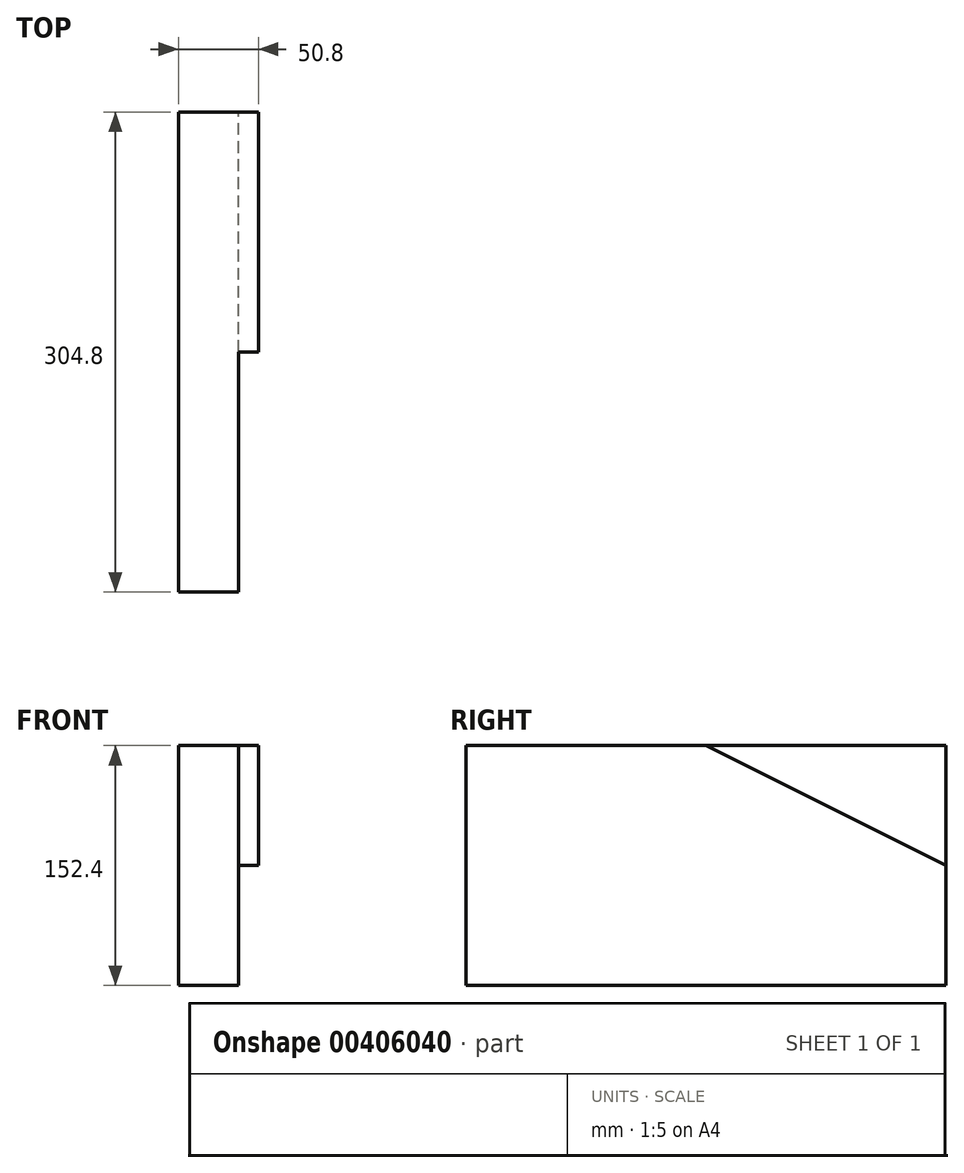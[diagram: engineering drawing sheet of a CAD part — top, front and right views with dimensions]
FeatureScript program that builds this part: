
annotation { "Feature Type Name" : "Feature", "Feature Type Description" : "" }
export const myFeature = defineFeature(function(context is Context, id is Id, definition is map)
    precondition{}
    {
        {
            var Q0;
            Q0=qCreatedBy(makeId("Right.planeOp"),FACE);
            var sketch = newSketch(context, id + "F0", { "sketchPlane" : qUnion([Q0])});
            skLineSegment(sketch, "E0.bottom", {"start": v(152.4, -76.2) * mm, "end": v(-152.4, -76.2) * mm});
            skLineSegment(sketch, "E0.top", {"start": v(152.4, 76.2) * mm, "end": v(-152.4, 76.2) * mm});
            skLineSegment(sketch, "E0.left", {"start": v(152.4, -76.2) * mm, "end": v(152.4, 76.2) * mm});
            skLineSegment(sketch, "E0.right", {"start": v(-152.4, -76.2) * mm, "end": v(-152.4, 76.2) * mm});
            skPoint(sketch, "E0.middle", {"position": v(0, 0) * mm});
            skSolve(sketch);
        }
        {
            var Q0;
            Q0=makeQuery(id+"F0.imprint","IMPRINT",FACE,{"disambiguationData":[TD([[makeQuery(id+"F0.imprint","IMPRINT",EDGE,{"derivedFrom":sQuery(id+"F0.wireOp",EDGE,"E0.bottom")}),-1.0]])]});
            extrude(context, id + "F1", {"entities" : qUnion([Q0]), "depth" : 6.35 * mm});
        }
        {
            var Q0;
            Q0=makeQuery(id+"F1.opExtrude","CAP_FACE",FACE,{"disambiguationData":[OSD([sQuery(id+"F0.wireOp",EDGE,"E0.bottom"),sQuery(id+"F0.wireOp",EDGE,"E0.top"),sQuery(id+"F0.wireOp",EDGE,"E0.left"),sQuery(id+"F0.wireOp",EDGE,"E0.right")])],"isStart":false});
            var sketch = newSketch(context, id + "F2", { "sketchPlane" : qUnion([Q0])});
            skLineSegment(sketch, "E1.bottom", {"start": v(152.4, -76.2) * mm, "end": v(-152.4, -76.2) * mm});
            skLineSegment(sketch, "E1.top", {"start": v(152.4, 76.2) * mm, "end": v(-152.4, 76.2) * mm});
            skLineSegment(sketch, "E1.left", {"start": v(152.4, -76.2) * mm, "end": v(152.4, 76.2) * mm});
            skLineSegment(sketch, "E1.right", {"start": v(-152.4, -76.2) * mm, "end": v(-152.4, 76.2) * mm});
            skPoint(sketch, "E1.middle", {"position": v(0, 0) * mm});
            skLineSegment(sketch, "E2", {"start": v(0, 76.2) * mm, "end": v(152.4, 0) * mm});
            skSolve(sketch);
        }
        {
            var Q0;
            {var subQ1=sQuery(id+"F2.wireOp",EDGE,"E1.bottom");Q0=makeQuery(id+"F2.imprint","IMPRINT",FACE,{"disambiguationData":[TD([[makeQuery(id+"F2.imprint","IMPRINT",EDGE,{"derivedFrom":subQ1}),-1.0]])]});}
            extrude(context, id + "F3", {"entities" : qUnion([Q0]), "operationType" : NewBodyOperationType.ADD, "depth" : 6.35 * mm});
        }
        {
            var Q0;
            Q0=makeQuery(id+"F1.opExtrude","CAP_FACE",FACE,{"disambiguationData":[OSD([sQuery(id+"F0.wireOp",EDGE,"E0.bottom"),sQuery(id+"F0.wireOp",EDGE,"E0.top"),sQuery(id+"F0.wireOp",EDGE,"E0.left"),sQuery(id+"F0.wireOp",EDGE,"E0.right")])],"isStart":true});
            var sketch = newSketch(context, id + "F4", { "sketchPlane" : qUnion([Q0])});
            skLineSegment(sketch, "E3.bottom", {"start": v(152.4, -76.2) * mm, "end": v(-152.4, -76.2) * mm});
            skLineSegment(sketch, "E3.top", {"start": v(152.4, 76.2) * mm, "end": v(-152.4, 76.2) * mm});
            skLineSegment(sketch, "E3.left", {"start": v(152.4, -76.2) * mm, "end": v(152.4, 76.2) * mm});
            skLineSegment(sketch, "E3.right", {"start": v(-152.4, -76.2) * mm, "end": v(-152.4, 76.2) * mm});
            skPoint(sketch, "E3.middle", {"position": v(0, 0) * mm});
            skLineSegment(sketch, "E4", {"start": v(0, 76.2) * mm, "end": v(-152.4, 0) * mm});
            skSolve(sketch);
        }
        {
            var Q0;
            {var subQ3=sQuery(id+"F4.wireOp",EDGE,"E4");Q0=makeQuery(id+"F4.imprint","IMPRINT",FACE,{"disambiguationData":[TD([[makeQuery(id+"F4.imprint","IMPRINT",EDGE,{"derivedFrom":subQ3}),-1.0]])]});}
            extrude(context, id + "F5", {"entities" : qUnion([Q0]), "operationType" : NewBodyOperationType.ADD, "oppositeDirection" : true, "depth" : 25.4 * mm});
        }
        {
            var Q0;
            Q0=makeQuery(id+"F1.opExtrude","CAP_FACE",FACE,{"disambiguationData":[OSD([sQuery(id+"F0.wireOp",EDGE,"E0.bottom"),sQuery(id+"F0.wireOp",EDGE,"E0.top"),sQuery(id+"F0.wireOp",EDGE,"E0.left"),sQuery(id+"F0.wireOp",EDGE,"E0.right")])],"isStart":true});
            extrude(context, id + "F6", {"entities" : qUnion([Q0]), "operationType" : NewBodyOperationType.ADD, "depth" : 25.4 * mm});
        }
    });
